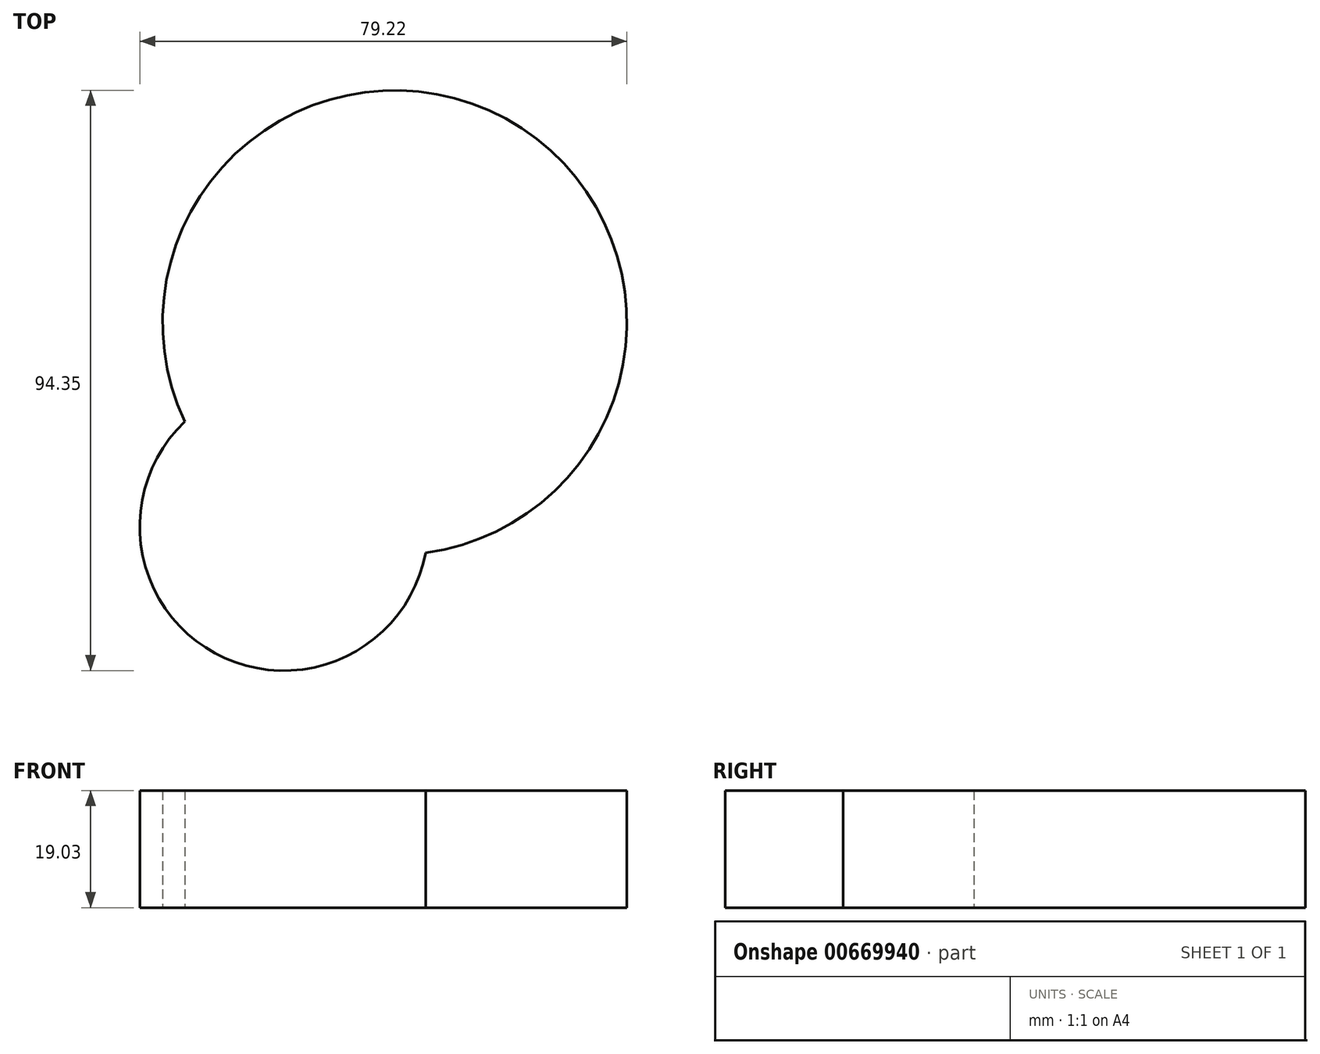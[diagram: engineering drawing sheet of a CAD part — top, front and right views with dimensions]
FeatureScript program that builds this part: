
annotation { "Feature Type Name" : "Feature", "Feature Type Description" : "" }
export const myFeature = defineFeature(function(context is Context, id is Id, definition is map)
    precondition{}
    {
        {
            var Q0;
            Q0=qCreatedBy(makeId("Top.planeOp"),FACE);
            var sketch = newSketch(context, id + "F0", { "sketchPlane" : qUnion([Q0])});
            skCircle(sketch, "E0", {"center": v(-4.4, -8.74) * mm, "radius": 23.44 * mm});
            skPoint(sketch, "E0.first.point", {"position": v(16.24, -19.85) * mm});
            skPoint(sketch, "E0.second.point", {"position": v(17.35, 0) * mm});
            skPoint(sketch, "E0.third.point", {"position": v(0, 14.29) * mm});
            skCircle(sketch, "E1", {"center": v(13.64, 24.43) * mm, "radius": 37.75 * mm});
            skPoint(sketch, "E1.first.point", {"position": v(-24.1, 23.82) * mm});
            skPoint(sketch, "E1.third.point", {"position": v(-9.85, 53.97) * mm});
            skSolve(sketch);
        }
        {
            var Q0;
            Q0 = qSketchRegion(id + "F0", true);
            extrude(context, id + "F1", {"entities" : qUnion([Q0]), "depth" : 19.03 * mm, "offsetDistance" : 25.4 * mm});
        }
    });
